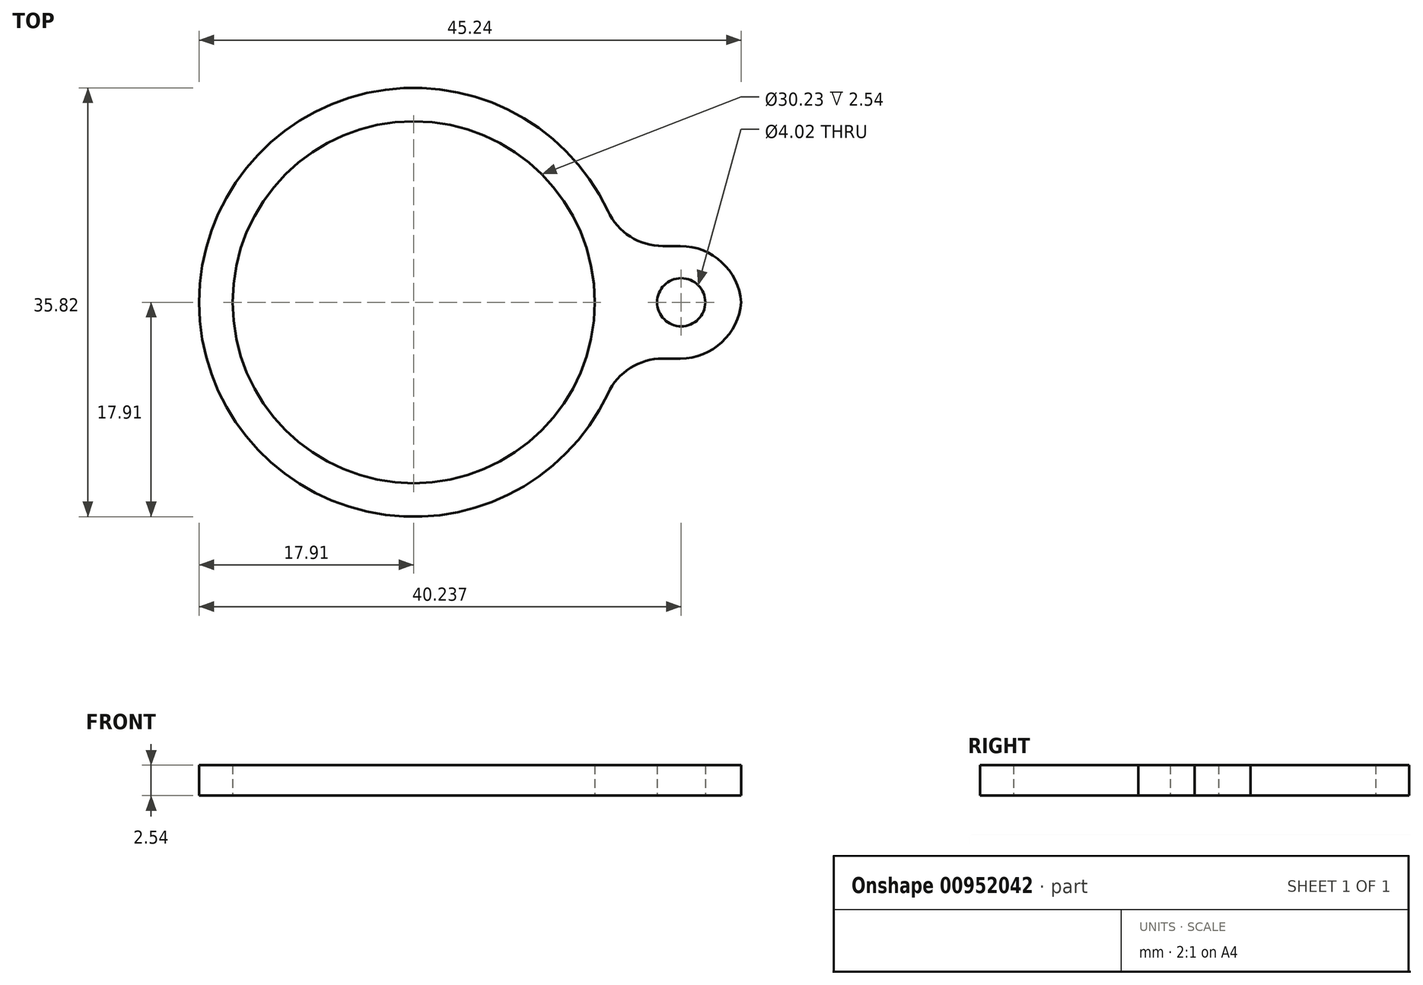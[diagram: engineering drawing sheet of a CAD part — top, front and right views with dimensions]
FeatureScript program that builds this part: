
annotation { "Feature Type Name" : "Feature", "Feature Type Description" : "" }
export const myFeature = defineFeature(function(context is Context, id is Id, definition is map)
    precondition{}
    {
        {
            var Q0;
            Q0=qCreatedBy(makeId("Top.planeOp"),FACE);
            var sketch = newSketch(context, id + "F0", { "sketchPlane" : qUnion([Q0])});
            skCircle(sketch, "E0", {"center": v(0, 0) * mm, "radius": 15.11 * mm});
            skArc(sketch, "E1", {"start": v(17.28, 4.7) * mm, "mid": v(-17.9, 0) * mm, "end": v(17.28, -4.7) * mm});
            skLineSegment(sketch, "E2.bottom", {"start": v(17.28, 4.7) * mm, "end": v(27.35, 4.7) * mm});
            skLineSegment(sketch, "E2.top", {"start": v(17.28, -4.7) * mm, "end": v(27.35, -4.7) * mm});
            skLineSegment(sketch, "E2.right", {"start": v(27.35, 4.7) * mm, "end": v(27.35, -4.7) * mm});
            skCircle(sketch, "E3", {"center": v(22.33, 0) * mm, "radius": 2.01 * mm});
            skSolve(sketch);
        }
        {
            var Q0;
            Q0=makeQuery(id+"F0.imprint","IMPRINT",FACE,{"disambiguationData":[TD([[makeQuery(id+"F0.imprint","IMPRINT",EDGE,{"derivedFrom":sQuery(id+"F0.wireOp",EDGE,"E0")}),-1.0]])]});
            extrude(context, id + "F1", {"entities" : qUnion([Q0]), "depth" : 2.54 * mm, "offsetDistance" : 25.4 * mm});
        }
        {
            var Q0;
            Q0=makeQuery(id+"F1.opExtrude","SWEPT_EDGE",EDGE,{"disambiguationData":[OSD([sQuery(id+"F0.wireOp",EDGE,"E1"),sQuery(id+"F0.wireOp",EDGE,"E2.bottom")])]});
            var Q1;
            Q1=makeQuery(id+"F1.opExtrude","SWEPT_EDGE",EDGE,{"disambiguationData":[OSD([sQuery(id+"F0.wireOp",EDGE,"E1"),sQuery(id+"F0.wireOp",EDGE,"E2.top")])]});
            var Q2;
            Q2=makeQuery(id+"F1.opExtrude","SWEPT_EDGE",EDGE,{"disambiguationData":[OSD([sQuery(id+"F0.wireOp",EDGE,"E2.top"),sQuery(id+"F0.wireOp",EDGE,"E2.right")])]});
            var Q3;
            Q3=makeQuery(id+"F1.opExtrude","SWEPT_EDGE",EDGE,{"disambiguationData":[OSD([sQuery(id+"F0.wireOp",EDGE,"E2.bottom"),sQuery(id+"F0.wireOp",EDGE,"E2.right")])]});
            fillet(context, id + "F2", {"entities" : qUnion([Q0, Q1, Q2, Q3]), "radius" : 5.08 * mm, "tangentPropagation" : true, "allowEdgeOverflow" : false});
        }
    });
